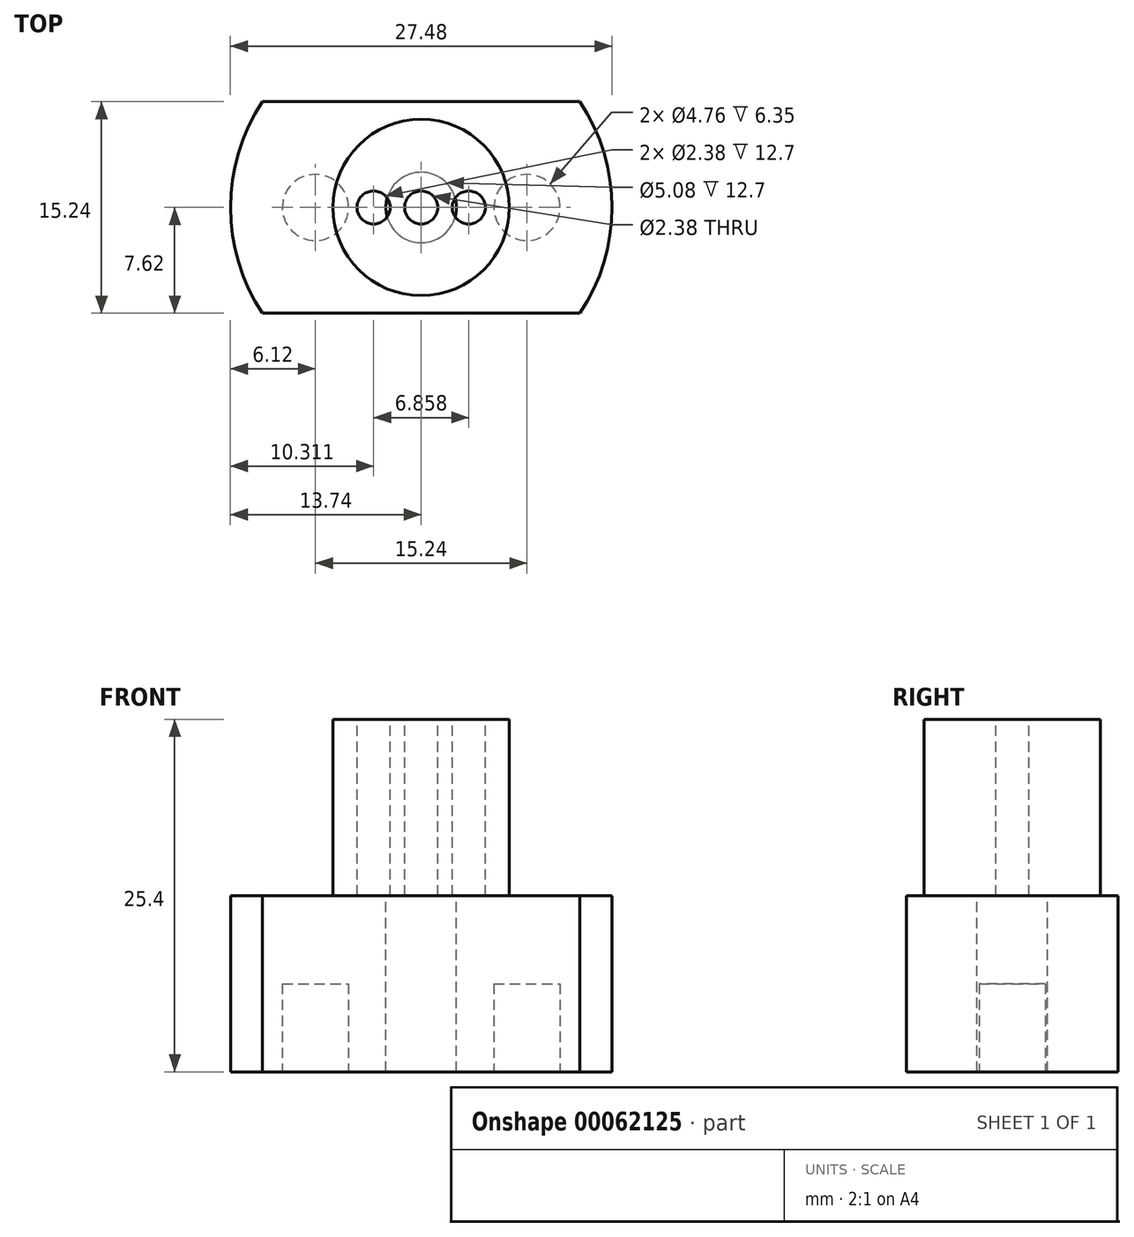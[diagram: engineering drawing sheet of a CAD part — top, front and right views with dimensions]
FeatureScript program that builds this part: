
annotation { "Feature Type Name" : "Feature", "Feature Type Description" : "" }
export const myFeature = defineFeature(function(context is Context, id is Id, definition is map)
    precondition{}
    {
        {
            var Q0;
            Q0=qCreatedBy(makeId("Top.planeOp"),FACE);
            var sketch = newSketch(context, id + "F0", { "sketchPlane" : qUnion([Q0])});
            skLineSegment(sketch, "E0.rect.bottom", {"start": v(11.43, -7.62) * mm, "end": v(-11.43, -7.62) * mm});
            skLineSegment(sketch, "E0.rect.top", {"start": v(11.43, 7.62) * mm, "end": v(-11.43, 7.62) * mm});
            skPoint(sketch, "E0.rect.middle", {"position": v(0, 0) * mm});
            skArc(sketch, "E1", {"start": v(-11.43, 7.62) * mm, "mid": v(-13.74, 0) * mm, "end": v(-11.43, -7.62) * mm});
            skArc(sketch, "E2", {"start": v(11.43, 7.62) * mm, "mid": v(13.74, 0) * mm, "end": v(11.43, -7.62) * mm});
            skSolve(sketch);
        }
        {
            var Q0;
            Q0=qSketchRegion(id+"F0",true);
            extrude(context, id + "F1", {"entities" : qUnion([Q0]), "depth" : 12.7 * mm});
        }
        {
            var Q0;
            Q0=makeQuery(id+"F1.opExtrude","CAP_FACE",FACE,{"disambiguationData":[OSD([sQuery(id+"F0.wireOp",EDGE,"E0.rect.bottom"),sQuery(id+"F0.wireOp",EDGE,"E0.rect.top"),sQuery(id+"F0.wireOp",EDGE,"E1"),sQuery(id+"F0.wireOp",EDGE,"E2")])],"isStart":false});
            var sketch = newSketch(context, id + "F2", { "sketchPlane" : qUnion([Q0])});
            skCircle(sketch, "E3", {"center": v(0, 0) * mm, "radius": 2.54 * mm});
            skSolve(sketch);
        }
        {
            var Q0;
            Q0=qSketchRegion(id+"F2",true);
            extrude(context, id + "F3", {"entities" : qUnion([Q0]), "operationType" : NewBodyOperationType.REMOVE, "endBound" : BoundingType.THROUGH_ALL, "oppositeDirection" : true, "depth" : 25.4 * mm});
        }
        {
            var Q0;
            Q0=makeQuery(id+"F1.opExtrude","CAP_FACE",FACE,{"disambiguationData":[OSD([sQuery(id+"F0.wireOp",EDGE,"E0.rect.bottom"),sQuery(id+"F0.wireOp",EDGE,"E0.rect.top"),sQuery(id+"F0.wireOp",EDGE,"E1"),sQuery(id+"F0.wireOp",EDGE,"E2")])],"isStart":false});
            var sketch = newSketch(context, id + "F4", { "sketchPlane" : qUnion([Q0])});
            skCircle(sketch, "E4", {"center": v(0, 0) * mm, "radius": 6.35 * mm});
            skSolve(sketch);
        }
        {
            var Q0;
            Q0=qSketchRegion(id+"F4",true);
            extrude(context, id + "F5", {"entities" : qUnion([Q0]), "operationType" : NewBodyOperationType.ADD, "depth" : 12.7 * mm});
        }
        {
            var Q0;
            Q0=makeQuery(id+"F1.opExtrude","CAP_FACE",FACE,{"disambiguationData":[OSD([sQuery(id+"F0.wireOp",EDGE,"E0.rect.bottom"),sQuery(id+"F0.wireOp",EDGE,"E0.rect.top"),sQuery(id+"F0.wireOp",EDGE,"E1"),sQuery(id+"F0.wireOp",EDGE,"E2")])],"isStart":true});
            var sketch = newSketch(context, id + "F6", { "sketchPlane" : qUnion([Q0])});
            skCircle(sketch, "E5", {"center": v(-7.62, 0) * mm, "radius": 2.38 * mm});
            skCircle(sketch, "E6", {"center": v(7.62, 0) * mm, "radius": 2.38 * mm});
            skSolve(sketch);
        }
        {
            var Q0;
            Q0=makeQuery(id+"F6.imprint","IMPRINT",FACE,{"disambiguationData":[TD([[makeQuery(id+"F6.imprint","IMPRINT",EDGE,{"derivedFrom":sQuery(id+"F6.wireOp",EDGE,"E5")}),1.0]])]});
            var Q1;
            Q1=makeQuery(id+"F6.imprint","IMPRINT",FACE,{"disambiguationData":[TD([[makeQuery(id+"F6.imprint","IMPRINT",EDGE,{"derivedFrom":sQuery(id+"F6.wireOp",EDGE,"E6")}),1.0]])]});
            extrude(context, id + "F7", {"entities" : qUnion([Q0, Q1]), "operationType" : NewBodyOperationType.REMOVE, "oppositeDirection" : true, "depth" : 6.35 * mm});
        }
        {
            var Q0;
            Q0=makeQuery(id+"F5.opExtrude","CAP_FACE",FACE,{"disambiguationData":[OSD([sQuery(id+"F4.wireOp",EDGE,"E4")])],"isStart":false});
            var sketch = newSketch(context, id + "F8", { "sketchPlane" : qUnion([Q0])});
            skCircle(sketch, "E7", {"center": v(-3.43, 0) * mm, "radius": 1.2 * mm});
            skCircle(sketch, "E8", {"center": v(3.43, 0) * mm, "radius": 1.2 * mm});
            skCircle(sketch, "E9", {"center": v(0, 0) * mm, "radius": 1.2 * mm});
            skSolve(sketch);
        }
        {
            var Q0;
            Q0=makeQuery(id+"F8.imprint","IMPRINT",FACE,{"disambiguationData":[TD([[makeQuery(id+"F8.imprint","IMPRINT",EDGE,{"derivedFrom":sQuery(id+"F8.wireOp",EDGE,"E7")}),1.0]])]});
            var Q1;
            Q1=makeQuery(id+"F8.imprint","IMPRINT",FACE,{"disambiguationData":[TD([[makeQuery(id+"F8.imprint","IMPRINT",EDGE,{"derivedFrom":sQuery(id+"F8.wireOp",EDGE,"E8")}),1.0]])]});
            var Q2;
            Q2=makeQuery(id+"F8.imprint","IMPRINT",FACE,{"disambiguationData":[TD([[makeQuery(id+"F8.imprint","IMPRINT",EDGE,{"derivedFrom":sQuery(id+"F8.wireOp",EDGE,"E9")}),1.0]])]});
            extrude(context, id + "F9", {"entities" : qUnion([Q0, Q1, Q2]), "operationType" : NewBodyOperationType.REMOVE, "oppositeDirection" : true, "depth" : 12.7 * mm});
        }
    });
